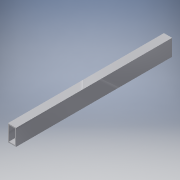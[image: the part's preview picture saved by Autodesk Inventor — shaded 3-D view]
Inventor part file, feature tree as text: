
AUTODESK INVENTOR PART (.ipt)
format: ipt  version: 2016 (Build 200138000, 138)  size: 109,056 bytes
history: native  units: in
note: dims shown in document units (in); Inventor stores cm internally (conversion verified against a paired STEP export)
features: extrude x1, sketch x1
ambient origin geometry x8: Origin, YZ Plane, XZ Plane, XY Plane, X Axis, Y Axis, Z Axis, Center Point
bodies: Solid1 (feature_tree)
feature tree (2):
  extrude  "Extrusion1"  Depth=2.0in
  sketch  "Sketch1"  dims[d0=1.0in d1=2.0in d2=0.125in d3=19.0in d4=0.0in]
